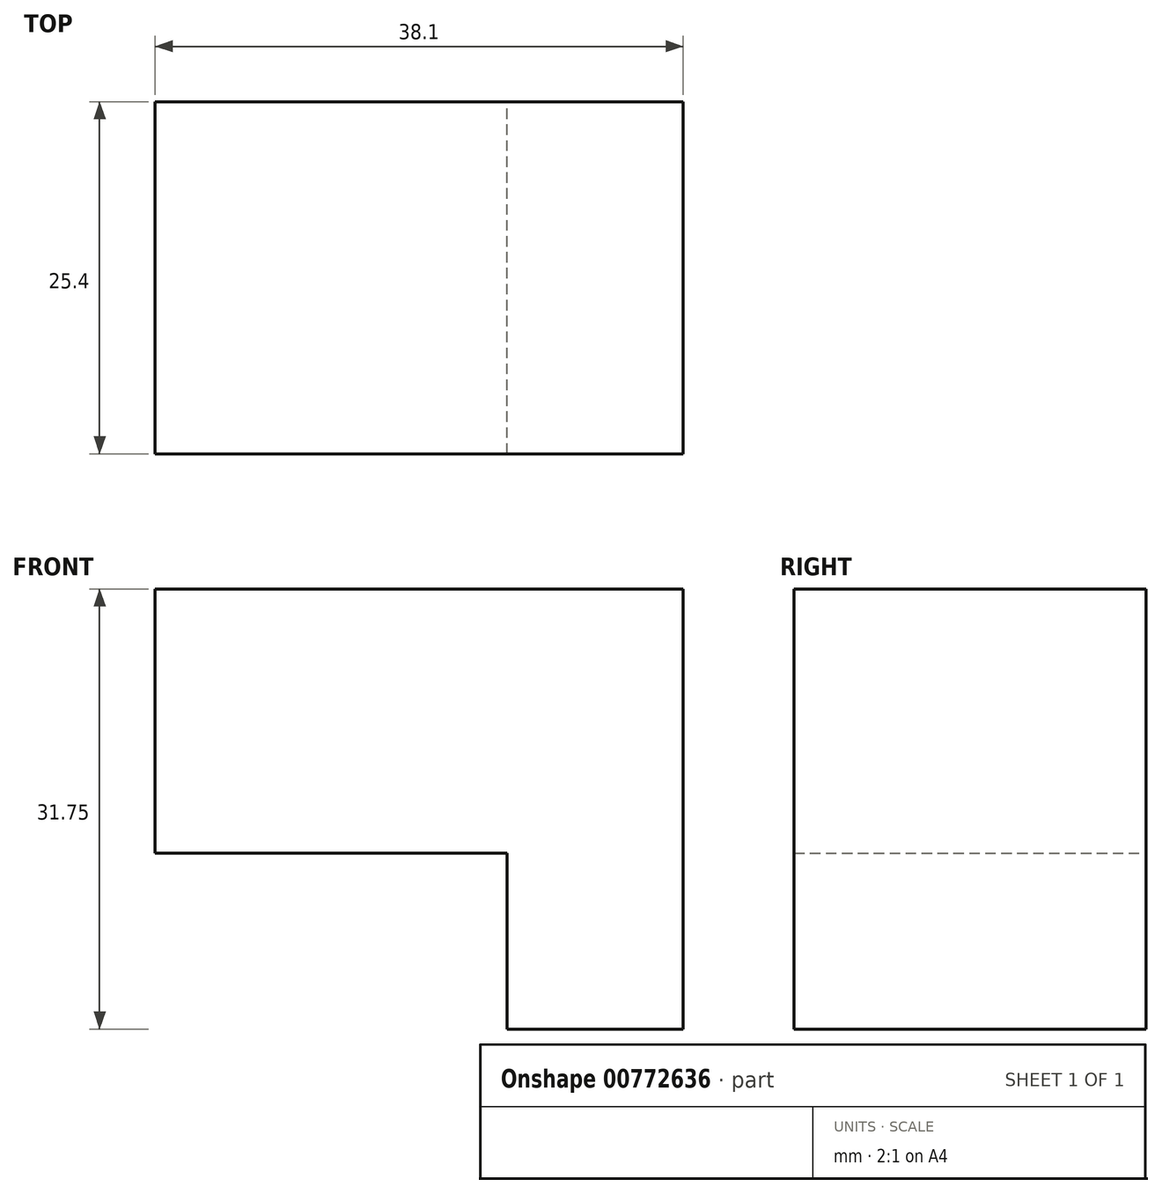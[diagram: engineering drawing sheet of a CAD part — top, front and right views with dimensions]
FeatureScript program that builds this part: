
annotation { "Feature Type Name" : "Feature", "Feature Type Description" : "" }
export const myFeature = defineFeature(function(context is Context, id is Id, definition is map)
    precondition{}
    {
        {
            var Q0;
            Q0=qCreatedBy(makeId("Front.planeOp"),FACE);
            var sketch = newSketch(context, id + "F0", { "sketchPlane" : qUnion([Q0])});
            skLineSegment(sketch, "E0", {"start": v(0, 0) * mm, "end": v(38.1, 0) * mm});
            skLineSegment(sketch, "E1", {"start": v(38.1, 0) * mm, "end": v(38.1, 121.4) * mm});
            skLineSegment(sketch, "E2", {"start": v(38.1, 0) * mm, "end": v(38.1, 31.75) * mm});
            skLineSegment(sketch, "E3", {"start": v(38.1, 31.75) * mm, "end": v(0, 31.75) * mm});
            skLineSegment(sketch, "E4", {"start": v(0, 0) * mm, "end": v(0, 31.75) * mm});
            skSolve(sketch);
        }
        {
            var Q0;
            Q0=makeQuery(id+"F0.imprint","IMPRINT",FACE,{"disambiguationData":[TD([[makeQuery(id+"F0.imprint","IMPRINT",EDGE,{"derivedFrom":sQuery(id+"F0.wireOp",EDGE,"E0")}),1.0]])]});
            extrude(context, id + "F1", {"entities" : qUnion([Q0]), "depth" : 25.4 * mm, "offsetDistance" : 25.4 * mm});
        }
        {
            var Q0;
            Q0=qCreatedBy(makeId("Right.planeOp"),FACE);
            var sketch = newSketch(context, id + "F2", { "sketchPlane" : qUnion([Q0])});
            skLineSegment(sketch, "E5", {"start": v(0, 0) * mm, "end": v(0, 12.7) * mm});
            skLineSegment(sketch, "E6", {"start": v(0, 12.7) * mm, "end": v(-25.38, 12.7) * mm});
            skLineSegment(sketch, "E7", {"start": v(-25.38, 12.7) * mm, "end": v(-25.38, 0) * mm});
            skLineSegment(sketch, "E8", {"start": v(-25.38, 0) * mm, "end": v(0, 0) * mm});
            skSolve(sketch);
        }
        {
            var Q0;
            Q0=makeQuery(id+"F2.imprint","IMPRINT",FACE,{"disambiguationData":[TD([[makeQuery(id+"F2.imprint","IMPRINT",EDGE,{"derivedFrom":sQuery(id+"F2.wireOp",EDGE,"E5")}),1.0]])]});
            extrude(context, id + "F3", {"entities" : qUnion([Q0]), "operationType" : NewBodyOperationType.REMOVE, "depth" : 25.4 * mm, "offsetDistance" : 25.4 * mm});
        }
        {
            var Q0;
            Q0=makeQuery(id+"F3.boolean.opBoolean","COPY",FACE,{"derivedFrom":makeQuery(id+"F3.opExtrude","SWEPT_FACE",FACE,{"disambiguationData":[OSD([sQuery(id+"F2.wireOp",EDGE,"E7")])]})});
            extrude(context, id + "F4", {"entities" : qUnion([Q0]), "operationType" : NewBodyOperationType.ADD, "depth" : 25.4 * mm, "offsetDistance" : 25.4 * mm});
        }
        {
            var Q0;
            Q0=makeQuery(id+"F4.opExtrude","CAP_FACE",FACE,{"disambiguationData":[OSD([sQuery(id+"F2.wireOp",EDGE,"E7")])],"isStart":false});
            extrude(context, id + "F5", {"entities" : qUnion([Q0]), "operationType" : NewBodyOperationType.REMOVE, "oppositeDirection" : true, "depth" : 25.4 * mm, "offsetDistance" : 25.4 * mm});
        }
        {
            var Q0;
            Q0=makeQuery(id+"F5.boolean.opBoolean","COPY",FACE,{"derivedFrom":makeQuery(id+"F5.opExtrude","CAP_FACE",FACE,{"disambiguationData":[OSD([sQuery(id+"F2.wireOp",EDGE,"E7")])],"isStart":false})});
            extrude(context, id + "F6", {"entities" : qUnion([Q0]), "operationType" : NewBodyOperationType.REMOVE, "oppositeDirection" : true, "depth" : 25.4 * mm, "offsetDistance" : 25.4 * mm});
        }
    });
